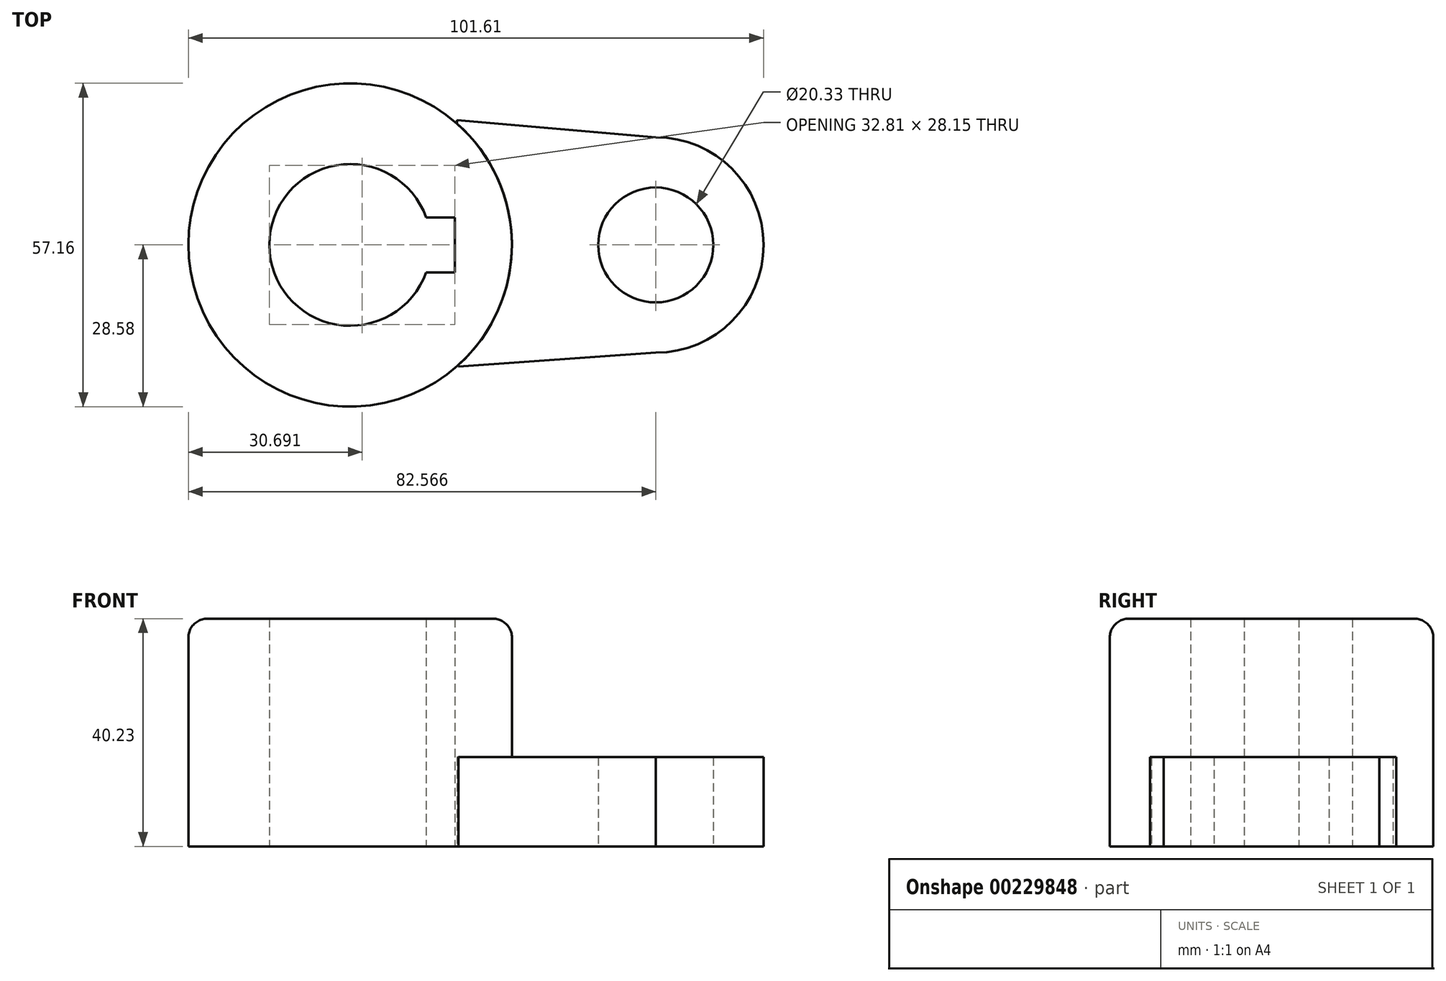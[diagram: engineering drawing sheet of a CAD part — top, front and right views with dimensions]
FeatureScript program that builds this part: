
annotation { "Feature Type Name" : "Feature", "Feature Type Description" : "" }
export const myFeature = defineFeature(function(context is Context, id is Id, definition is map)
    precondition{}
    {
        {
            var Q0;
            Q0=qCreatedBy(makeId("Top.planeOp"),FACE);
            var sketch = newSketch(context, id + "F0", { "sketchPlane" : qUnion([Q0])});
            skCircle(sketch, "E0", {"center": v(-45.4, 0) * mm, "radius": 28.58 * mm});
            skCircle(sketch, "E1", {"center": v(-45.4, 0) * mm, "radius": 14.29 * mm});
            skPoint(sketch, "E2.middle", {"position": v(-26.88, 0) * mm});
            skLineSegment(sketch, "E3", {"start": v(-26.88, 0) * mm, "end": v(-26.88, 4.83) * mm});
            skLineSegment(sketch, "E4", {"start": v(-26.88, 0) * mm, "end": v(-26.88, -4.84) * mm});
            skLineSegment(sketch, "E5", {"start": v(-26.88, -4.84) * mm, "end": v(-39.87, -4.84) * mm});
            skLineSegment(sketch, "E6", {"start": v(-26.88, 4.83) * mm, "end": v(-39.87, 4.83) * mm});
            skLineSegment(sketch, "E7", {"start": v(-39.87, 4.83) * mm, "end": v(-39.87, -4.84) * mm});
            skLineSegment(sketch, "E8", {"start": v(-45.4, 0) * mm, "end": v(8.58, 0) * mm});
            skPoint(sketch, "E9", {"position": v(8.58, 0) * mm});
            skSolve(sketch);
        }
        {
            var Q0;
            Q0 = qSketchRegion(id + "F0", true);
            extrude(context, id + "F1", {"entities" : qUnion([Q0]), "depth" : 40.23 * mm});
        }
        {
            var Q0;
            {var subQ4=sQuery(id+"F0.wireOp",EDGE,"E3");Q0=makeQuery(id+"F0.imprint","IMPRINT",FACE,{"disambiguationData":[TD([[makeQuery(id+"F0.imprint","IMPRINT",EDGE,{"derivedFrom":subQ4}),1.0]])]});}
            var Q1;
            {var subQ5=sQuery(id+"F0.wireOp",EDGE,"E7");Q1=makeQuery(id+"F0.imprint","IMPRINT",FACE,{"disambiguationData":[TD([[makeQuery(id+"F0.imprint","IMPRINT",EDGE,{"derivedFrom":subQ5}),-1.0]])]});}
            extrude(context, id + "F2", {"entities" : qUnion([Q0, Q1]), "operationType" : NewBodyOperationType.REMOVE, "depth" : 40.23 * mm});
        }
        {
            var Q0;
            Q0=makeQuery(id+"F1.opExtrude","CAP_EDGE",EDGE,{"disambiguationData":[OSD([sQuery(id+"F0.wireOp",EDGE,"E0")])],"isStart":false});
            fillet(context, id + "F3", {"entities" : qUnion([Q0]), "radius" : 3.3 * mm, "tangentPropagation" : true, "allowEdgeOverflow" : false});
        }
        {
            var Q0;
            Q0=qCreatedBy(makeId("Top.planeOp"),FACE);
            var sketch = newSketch(context, id + "F4", { "sketchPlane" : qUnion([Q0])});
            skPoint(sketch, "E10", {"position": v(8.6, 0) * mm});
            skCircle(sketch, "E11", {"center": v(8.6, 0) * mm, "radius": 10.16 * mm});
            skLineSegment(sketch, "E12.left", {"start": v(-26.53, 22.03) * mm, "end": v(-26.24, -21.48) * mm});
            skArc(sketch, "E13", {"start": v(8.6, -19.05) * mm, "mid": v(27.64, 0) * mm, "end": v(8.6, 19.05) * mm});
            skLineSegment(sketch, "E14", {"start": v(-26.53, 22.03) * mm, "end": v(8.6, 19.05) * mm});
            skLineSegment(sketch, "E15", {"start": v(-26.24, -21.48) * mm, "end": v(8.6, -19.05) * mm});
            skSolve(sketch);
        }
        {
            var Q0;
            Q0 = qSketchRegion(id + "F4", true);
            extrude(context, id + "F5", {"entities" : qUnion([Q0]), "operationType" : NewBodyOperationType.ADD, "depth" : 15.77 * mm});
        }
    });
